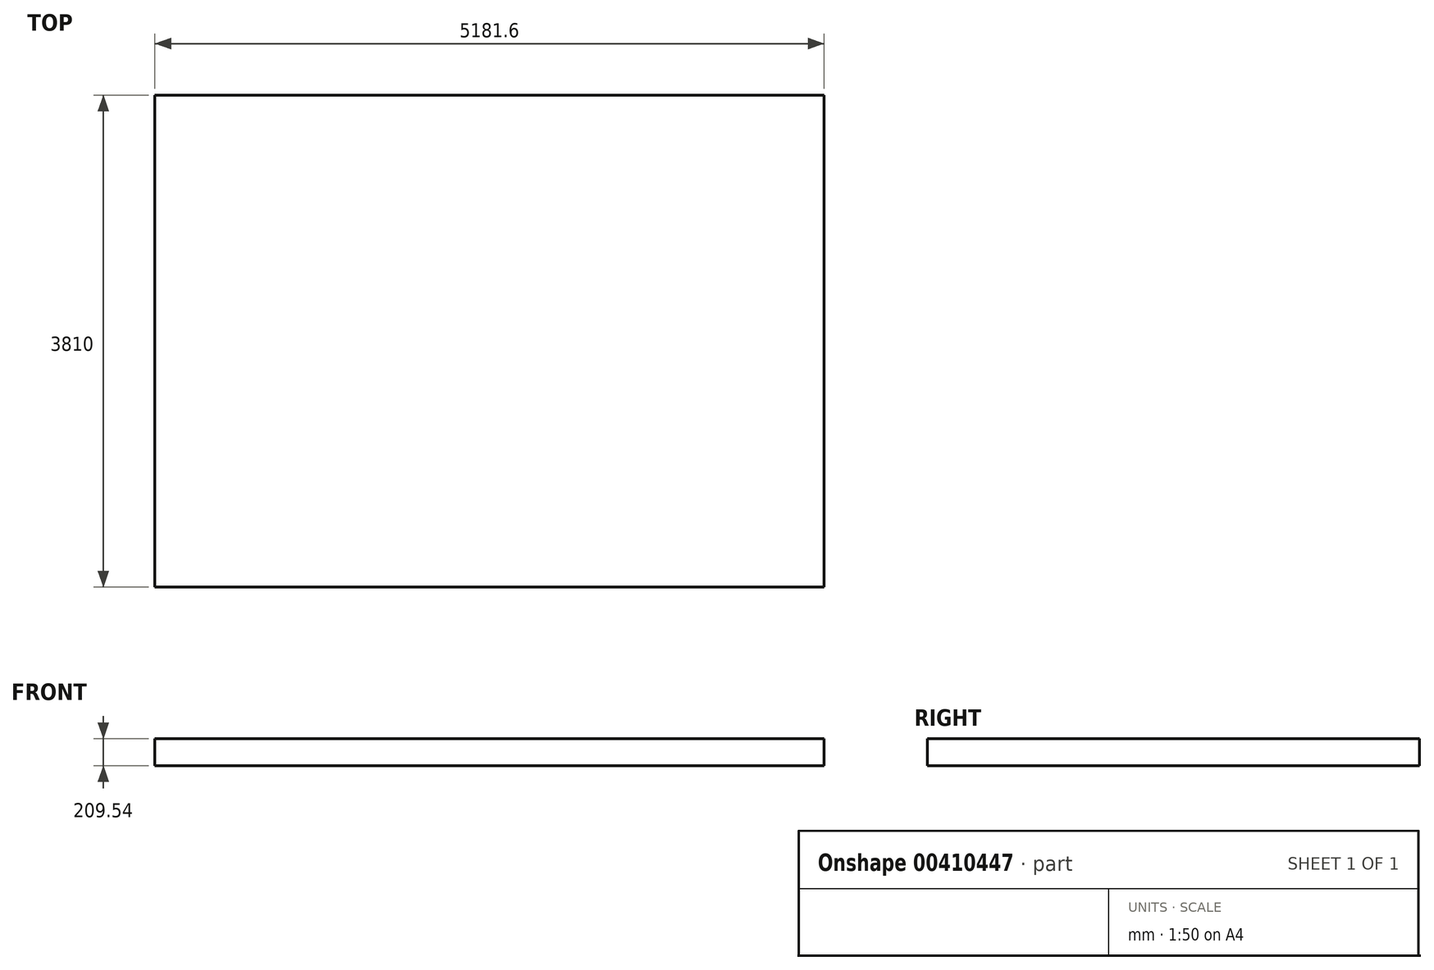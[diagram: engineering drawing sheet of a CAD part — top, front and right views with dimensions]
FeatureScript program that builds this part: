
annotation { "Feature Type Name" : "Feature", "Feature Type Description" : "" }
export const myFeature = defineFeature(function(context is Context, id is Id, definition is map)
    precondition{}
    {
        {
            var Q0;
            Q0=qCreatedBy(makeId("Right.planeOp"),FACE);
            var sketch = newSketch(context, id + "F0", { "sketchPlane" : qUnion([Q0])});
            skLineSegment(sketch, "E0.bottom", {"start": v(-1905, 104.77) * mm, "end": v(1905, 104.77) * mm});
            skLineSegment(sketch, "E0.top", {"start": v(-1905, -104.77) * mm, "end": v(1905, -104.77) * mm});
            skLineSegment(sketch, "E0.left", {"start": v(-1905, 104.77) * mm, "end": v(-1905, -104.77) * mm});
            skLineSegment(sketch, "E0.right", {"start": v(1905, 104.77) * mm, "end": v(1905, -104.77) * mm});
            skPoint(sketch, "E0.middle", {"position": v(0, 0) * mm});
            skSolve(sketch);
        }
        {
            var Q0;
            Q0 = qSketchRegion(id + "F0", true);
            extrude(context, id + "F1", {"entities" : qUnion([Q0]), "depth" : 5181.6 * mm, "offsetDistance" : 25.4 * mm});
        }
    });
